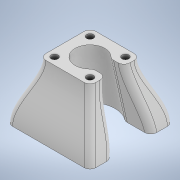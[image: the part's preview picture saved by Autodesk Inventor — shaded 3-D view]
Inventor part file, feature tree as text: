
AUTODESK INVENTOR PART (.ipt)
format: ipt  version: 2021 (Build 250183000, 183)  size: 354,816 bytes
history: native  units: mm
features: sketch x8, fillet x3, extrude x3, hole x3, other x2, plane x1, loft x1
ambient origin geometry x8: Origin, YZ Plane, XZ Plane, XY Plane, X Axis, Y Axis, Z Axis, Center Point
bodies: Body1 (feature_tree)
feature tree (21):
  other  "實體1"
  sketch  "草圖4"
  plane  "工作平面1"
  loft  "斷面混成1"
  fillet  "圓角2"  Radius=55.0mm
  extrude  "擠出3"  Depth=55.0mm
  fillet  "圓角3"  Radius=24.0mm
  hole  "孔2"  [1 undecoded]
  hole  "孔3"  [1 undecoded]
  extrude  "擠出1"  Depth=42.0mm
  extrude  "擠出2"  Depth=5.0mm
  hole  "孔1"  [1 undecoded]
  fillet  "圓角1"  Radius=70.0mm
  sketch  "草圖1"
  sketch  "草圖2"
  sketch  "草圖3"
  sketch  "草圖5"
  other  "實體2"
  sketch  "草圖6"
  sketch  "草圖7"
  sketch  "草圖8"
note: 3 required parameter values undecoded (feature->parameter linkage not recoverable at this tier; creation-order binding heuristic only, values carry confidence <= 0.55)
